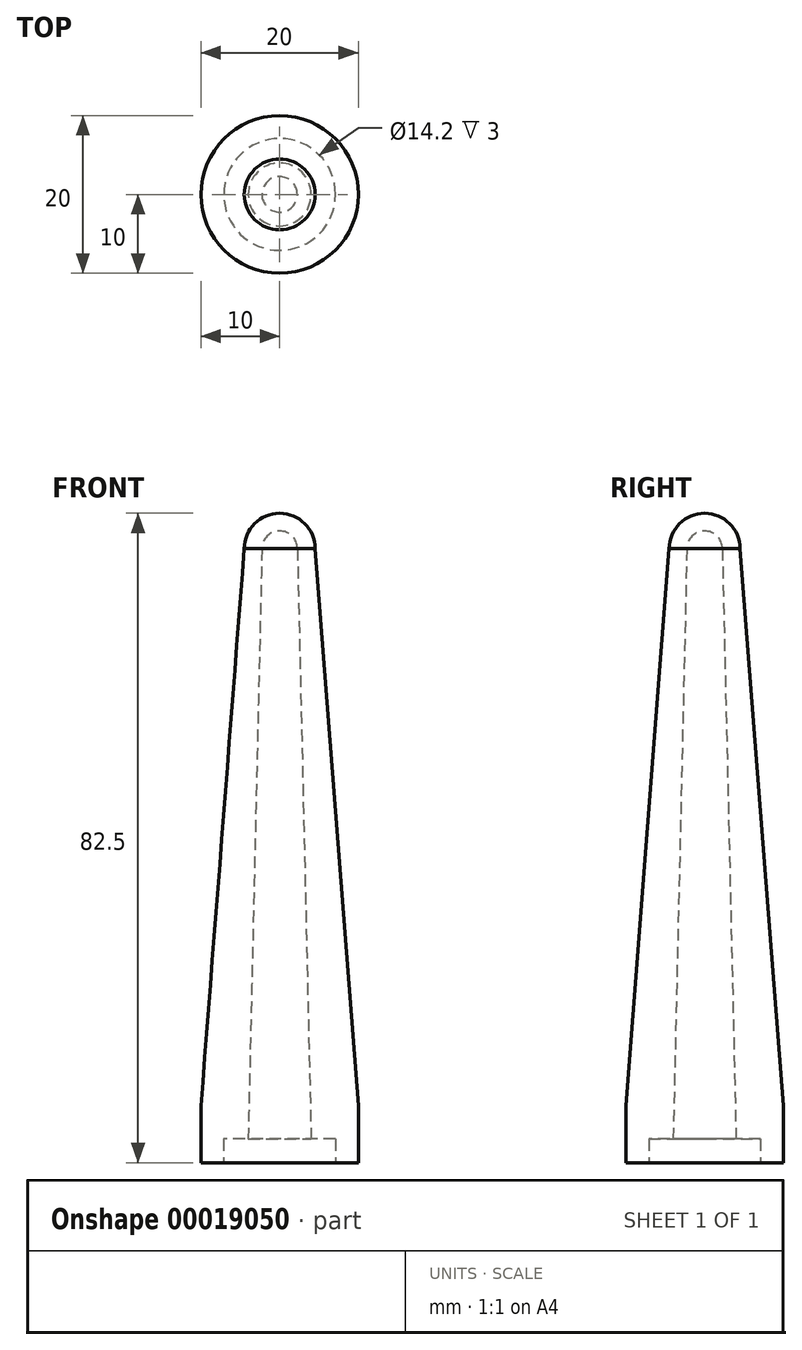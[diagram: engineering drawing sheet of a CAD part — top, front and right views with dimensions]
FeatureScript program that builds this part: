
annotation { "Feature Type Name" : "Feature", "Feature Type Description" : "" }
export const myFeature = defineFeature(function(context is Context, id is Id, definition is map)
    precondition{}
    {
        {
            var Q0;
            Q0=qCreatedBy(makeId("Top.planeOp"),FACE);
            var sketch = newSketch(context, id + "F0", { "sketchPlane" : qUnion([Q0])});
            skCircle(sketch, "E0", {"center": v(0, 0) * mm, "radius": 10 * mm});
            skCircle(sketch, "E1", {"center": v(0, 0) * mm, "radius": 7.1 * mm});
            skSolve(sketch);
        }
        {
            var Q0;
            Q0 = qSketchRegion(id + "F0", true);
            extrude(context, id + "F1", {"entities" : qUnion([Q0]), "depth" : 3 * mm});
        }
        {
            var Q0;
            Q0=makeQuery(id+"F1.opExtrude","CAP_FACE",FACE,{"disambiguationData":[OSD([sQuery(id+"F0.wireOp",EDGE,"E0"),sQuery(id+"F0.wireOp",EDGE,"E1")])],"isStart":false});
            var sketch = newSketch(context, id + "F2", { "sketchPlane" : qUnion([Q0])});
            skCircle(sketch, "E2", {"center": v(0, 0) * mm, "radius": 10 * mm});
            skSolve(sketch);
        }
        {
            var Q0;
            Q0=makeQuery(id+"F2.imprint","IMPRINT",FACE,{"disambiguationData":[TD([[makeQuery(id+"F2.imprint","IMPRINT",EDGE,{"derivedFrom":sQuery(id+"F2.wireOp",EDGE,"E2")}),1.0]])]});
            cPlane(context, id + "F3", {"entities" : qUnion([Q0]), "cplaneType" : CPlaneType.OFFSET, "offset" : 75 * mm, "width" : 150 * mm, "height" : 150 * mm});
        }
        {
            var Q0;
            Q0=qCreatedBy(id+"F3.planeOp",FACE);
            var sketch = newSketch(context, id + "F4", { "sketchPlane" : qUnion([Q0])});
            skCircle(sketch, "E3", {"center": v(0, 0) * mm, "radius": 4.5 * mm});
            skSolve(sketch);
        }
        {
            var Q0;
            Q0 = qSketchRegion(id + "F2", true);
            var Q1;
            Q1=makeQuery(id+"F2.imprint","IMPRINT",FACE,{"disambiguationData":[TD([[makeQuery(id+"F2.imprint","IMPRINT",EDGE,{"derivedFrom":sQuery(id+"F2.wireOp",EDGE,"E2")}),1.0]])]});
            extrude(context, id + "F5", {"entities" : qUnion([Q0, Q1]), "operationType" : NewBodyOperationType.ADD, "depth" : 4 * mm});
        }
        {
            var Q0;
            Q0=makeQuery(id+"F5.opExtrude","CAP_FACE",FACE,{"disambiguationData":[OSD([sQuery(id+"F2.wireOp",EDGE,"E2"),sQuery(id+"F2.wireOp",EDGE,"a812ff2d-9a64-46a3-aa2e-7564c3b67889")])],"isStart":false});
            var sketch = newSketch(context, id + "F6", { "sketchPlane" : qUnion([Q0])});
            skCircle(sketch, "E4", {"center": v(0, 0) * mm, "radius": 10 * mm});
            skSolve(sketch);
        }
        {
            var Q1;
            Q1=makeQuery(id+"F6.imprint","IMPRINT",FACE,{"disambiguationData":[TD([[makeQuery(id+"F6.imprint","IMPRINT",EDGE,{"derivedFrom":sQuery(id+"F6.wireOp",EDGE,"E4")}),1.0]])]});
            var Q2;
            Q2=makeQuery(id+"F4.imprint","IMPRINT",FACE,{"disambiguationData":[TD([[makeQuery(id+"F4.imprint","IMPRINT",EDGE,{"derivedFrom":sQuery(id+"F4.wireOp",EDGE,"E3")}),1.0]])]});
            loft(context, id + "F7", {"operationType" : NewBodyOperationType.ADD, "sheetProfilesArray" : [{ "sheetProfileEntities" : qUnion([Q1]) }, { "sheetProfileEntities" : qUnion([Q2]) }]});
        }
        {
            var Q0;
            Q0=makeQuery(id+"F5.opExtrude","CAP_FACE",FACE,{"disambiguationData":[OSD([sQuery(id+"F2.wireOp",EDGE,"E2")])],"isStart":true});
            var sketch = newSketch(context, id + "F8", { "sketchPlane" : qUnion([Q0])});
            skCircle(sketch, "E5", {"center": v(0, 0) * mm, "radius": 4 * mm});
            skSolve(sketch);
        }
        {
            var Q0;
            Q0=makeQuery(id+"F7.opLoft","CAP_FACE",FACE,{"disambiguationData":[OSD([makeQuery(id+"F4.imprint","IMPRINT",FACE,{"disambiguationData":[TD([[makeQuery(id+"F4.imprint","IMPRINT",EDGE,{"derivedFrom":sQuery(id+"F4.wireOp",EDGE,"E3")}),1.0]])]})])],"isStart":true});
            var sketch = newSketch(context, id + "F9", { "sketchPlane" : qUnion([Q0])});
            skCircle(sketch, "E6", {"center": v(0, 0) * mm, "radius": 2.25 * mm});
            skSolve(sketch);
        }
        {
            var Q1;
            Q1=makeQuery(id+"F8.imprint","IMPRINT",FACE,{"disambiguationData":[TD([[makeQuery(id+"F8.imprint","IMPRINT",EDGE,{"derivedFrom":sQuery(id+"F8.wireOp",EDGE,"E5")}),1.0]])]});
            var Q2;
            Q2=makeQuery(id+"F9.imprint","IMPRINT",FACE,{"disambiguationData":[TD([[makeQuery(id+"F9.imprint","IMPRINT",EDGE,{"derivedFrom":sQuery(id+"F9.wireOp",EDGE,"E6")}),1.0]])]});
            loft(context, id + "F10", {"operationType" : NewBodyOperationType.REMOVE, "sheetProfilesArray" : [{ "sheetProfileEntities" : qUnion([Q1]) }, { "sheetProfileEntities" : qUnion([Q2]) }]});
        }
        {
            var Q0;
            Q0=makeQuery(id+"F7.opLoft","CAP_FACE",FACE,{"disambiguationData":[OSD([makeQuery(id+"F4.imprint","IMPRINT",FACE,{"disambiguationData":[TD([[makeQuery(id+"F4.imprint","IMPRINT",EDGE,{"derivedFrom":sQuery(id+"F4.wireOp",EDGE,"E3")}),1.0]])]})])],"isStart":true});
            var sketch = newSketch(context, id + "F11", { "sketchPlane" : qUnion([Q0])});
            skCircle(sketch, "E7", {"center": v(0, 0) * mm, "radius": 4.5 * mm});
            skLineSegment(sketch, "E8", {"start": v(4.5, 0) * mm, "end": v(-4.5, 0) * mm});
            skSolve(sketch);
        }
        {
            var Q0;
            {var subQ1=sQuery(id+"F11.wireOp",EDGE,"E8");var subQ4=sQuery(id+"F11.wireOp",EDGE,"E7");var subQ6=makeQuery(id+"F11.imprint","INTERSECT",VERTEX,{"disambiguationData":[OD(0.0)],"derivedFrom":[subQ4,subQ1]});Q0=makeQuery(id+"F11.imprint","IMPRINT",FACE,{"disambiguationData":[TD([[makeQuery(id+"F11.imprint","IMPRINT",EDGE,{"disambiguationData":[TD([[subQ6,1.0]])],"derivedFrom":subQ4}),1.0]])]});}
            var Q1;
            Q1=sQuery(id+"F11.wireOp",EDGE,"E8");
            revolve(context, id + "F12", {"operationType" : NewBodyOperationType.ADD, "entities" : qUnion([Q0]), "axis" : qUnion([Q1]), "revolveType" : RevolveType.ONE_DIRECTION, "angle" : 180 * degree});
        }
        {
            var Q0;
            Q0=makeQuery(id+"F7.boolean.opBoolean","MERGE",EDGE,{"derivedFrom":[makeQuery(id+"F5.opExtrude","CAP_EDGE",EDGE,{"disambiguationData":[OSD([sQuery(id+"F2.wireOp",EDGE,"E2")])],"isStart":false}),makeQuery(id+"F7.opLoft","MID_CAP_EDGE",EDGE,{"disambiguationData":[OSD([sQuery(id+"F6.wireOp",EDGE,"E4")])],"capPos":0.0})]});
            fillet(context, id + "F13", {"entities" : qUnion([Q0]), "radius" : 5 * mm, "tangentPropagation" : true, "allowEdgeOverflow" : false});
        }
    });
